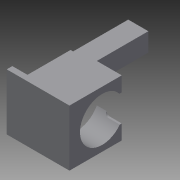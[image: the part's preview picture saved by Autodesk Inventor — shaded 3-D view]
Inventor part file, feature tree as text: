
AUTODESK INVENTOR PART (.ipt)
format: ipt  version: 2015 SP2 (Build 190223200, 223)  size: 165,888 bytes
history: native  units: mm
features: sketch x16, extrude x7, hole x2
ambient origin geometry x8: Origin, YZ Plane, XZ Plane, XY Plane, X Axis, Y Axis, Z Axis, Center Point
bodies: Solid1 (feature_tree)
feature tree (25):
  extrude  "Extrusion1"  Depth=31.0mm
  sketch  "Sketch2"  dims[d2=60.0mm d3=0.0mm d5=55.0mm]
  hole  "Hole1"  [1 undecoded]
  sketch  "Sketch4"  dims[d42=8.0mm d43=8.0mm]
  sketch  "Sketch5"  dims[d44=4.0mm d45=0.0mm d46=4.0mm d47=0.0mm]
  sketch  "Sketch7"  dims[d48=5.0mm d49=6.0mm d50=4.0mm d51=2.0mm d52=90.0deg d53=14.0mm d54=0.0mm d57=47.0mm]
  sketch  "Sketch8"  dims[d63=2.0mm d64=0.0mm d67=5.0mm d68=0.0mm]
  sketch  "Sketch9"  dims[d120=25.0mm d121=23.0mm]
  sketch  "Sketch14"  dims[d143=122.0mm d144=0.0mm d145=53.526mm d146=0.0mm]
  extrude  "Extrusion4"  Depth=4.0mm
  extrude  "Extrusion5"  Depth=8.0mm
  hole  "Hole5"  [1 undecoded]
  sketch  "Sketch18"  dims[d125=1.0mm]
  extrude  "Extrusion9"  Depth=47.0mm
  extrude  "Extrusion11"  Depth=5.0mm TaperAngle=0.0deg
  sketch  "Sketch29"
  sketch  "Sketch37"
  extrude  "Extrusion27"  Depth=23.0mm
  extrude  "Extrusion28"  Depth=53.526mm TaperAngle=0.0deg
  sketch  "Sketch1"  dims[d0=70.0mm d1=31.0mm]
  sketch  "Sketch3"  dims[d6=55.0mm d7=6.0mm d8=4.0mm d9=2.0mm d10=90.0deg d11=8.0mm d12=20.594885mm d33=4.0mm]
  sketch  "Sketch15"  dims[d124=1.0mm]
  sketch  "Sketch25"
  sketch  "Sketch39"
  sketch  "Sketch43"
note: 2 required parameter values undecoded (feature->parameter linkage not recoverable at this tier; creation-order binding heuristic only, values carry confidence <= 0.55)
